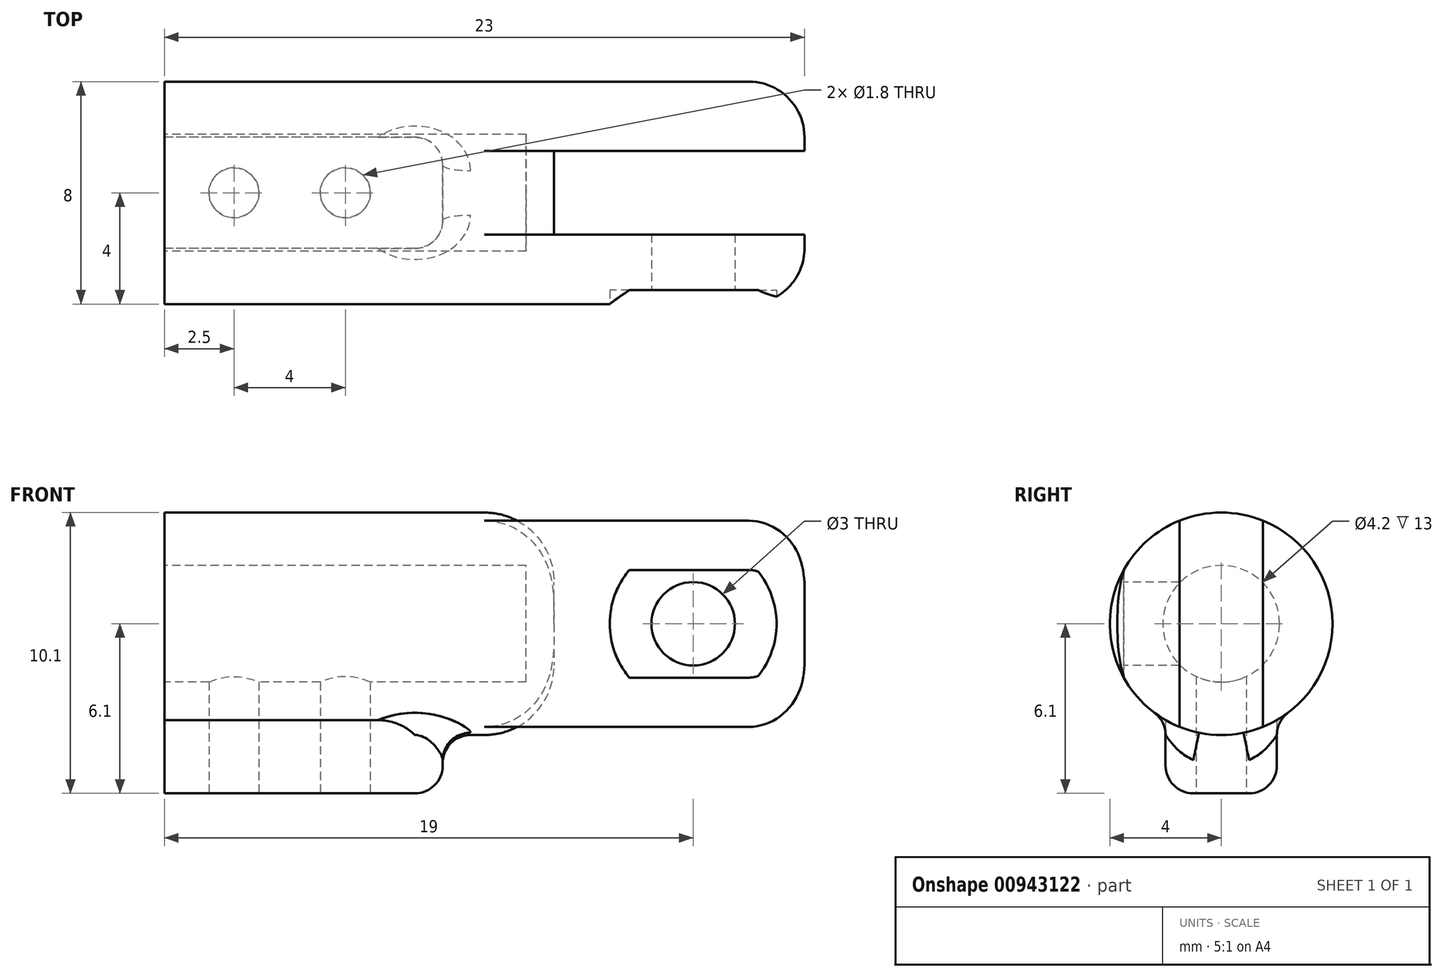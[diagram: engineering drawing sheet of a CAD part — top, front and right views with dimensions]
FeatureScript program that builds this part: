
annotation { "Feature Type Name" : "Feature", "Feature Type Description" : "" }
export const myFeature = defineFeature(function(context is Context, id is Id, definition is map)
    precondition{}
    {
        {
            var Q0;
            Q0=qCreatedBy(makeId("Right.planeOp"),FACE);
            var sketch = newSketch(context, id + "F0", { "sketchPlane" : qUnion([Q0])});
            skCircle(sketch, "E0", {"center": v(0, 0) * mm, "radius": 2.1 * mm});
            skCircle(sketch, "E1", {"center": v(0, 0) * mm, "radius": 4 * mm});
            skLineSegment(sketch, "E2", {"start": v(2, -3.46) * mm, "end": v(2, -6.1) * mm});
            skLineSegment(sketch, "E3", {"start": v(2, -6.1) * mm, "end": v(-2, -6.1) * mm});
            skLineSegment(sketch, "E4", {"start": v(-2, -6.1) * mm, "end": v(-2, -3.46) * mm});
            skSolve(sketch);
        }
        {
            var Q0;
            Q0=makeQuery(id+"F0.imprint","IMPRINT",FACE,{"disambiguationData":[TD([[makeQuery(id+"F0.imprint","IMPRINT",EDGE,{"derivedFrom":sQuery(id+"F0.wireOp",EDGE,"E0")}),-1.0]])]});
            var Q1;
            Q1=makeQuery(id+"F0.imprint","IMPRINT",FACE,{"disambiguationData":[TD([[makeQuery(id+"F0.imprint","IMPRINT",EDGE,{"derivedFrom":sQuery(id+"F0.wireOp",EDGE,"E0")}),1.0]])]});
            extrude(context, id + "F1", {"entities" : qUnion([Q0, Q1]), "depth" : 23 * mm, "offsetDistance" : 25 * mm});
        }
        {
            var Q0;
            Q0=makeQuery(id+"F0.imprint","IMPRINT",FACE,{"disambiguationData":[TD([[makeQuery(id+"F0.imprint","IMPRINT",EDGE,{"derivedFrom":sQuery(id+"F0.wireOp",EDGE,"E0")}),1.0]])]});
            extrude(context, id + "F2", {"entities" : qUnion([Q0]), "operationType" : NewBodyOperationType.REMOVE, "depth" : 13 * mm, "offsetDistance" : 25 * mm});
        }
        {
            var Q0;
            Q0=makeQuery(id+"F1.opExtrude","CAP_FACE",FACE,{"disambiguationData":[OSD([sQuery(id+"F0.wireOp",EDGE,"E0"),sQuery(id+"F0.wireOp",EDGE,"E1")])],"isStart":false});
            cPlane(context, id + "F3", {"entities" : qUnion([Q0]), "cplaneType" : CPlaneType.OFFSET, "offset" : 0 * mm, "width" : 150 * mm, "height" : 150 * mm});
        }
        {
            var Q0;
            Q0=qCreatedBy(id+"F3.planeOp",FACE);
            var sketch = newSketch(context, id + "F4", { "sketchPlane" : qUnion([Q0])});
            skLineSegment(sketch, "E5.bottom", {"start": v(1.5, -4) * mm, "end": v(-1.5, -4) * mm});
            skLineSegment(sketch, "E5.top", {"start": v(1.5, 4) * mm, "end": v(-1.5, 4) * mm});
            skLineSegment(sketch, "E5.left", {"start": v(1.5, -4) * mm, "end": v(1.5, 4) * mm});
            skLineSegment(sketch, "E5.right", {"start": v(-1.5, -4) * mm, "end": v(-1.5, 4) * mm});
            skPoint(sketch, "E5.middle", {"position": v(0, 0) * mm});
            skSolve(sketch);
        }
        {
            var Q0;
            {var subQ0=sQuery(id+"F4.wireOp",EDGE,"E5.left");var subQ1=sQuery(id+"F6oWoKsDEnx1sjk_1.wireOp",EDGE,"171556a4-600e-4862-a10e-88d223d029910.MirrorCS");var subQ2=sQuery(id+"F6oWoKsDEnx1sjk_1.wireOp",EDGE,"nGa1sqjB-H7Ow-3scy-iZwB-qixYv0Jmrafc.right");var subQ3=makeQuery(id+"FhGqZDnQz9BZsxH_1.opLoft","MID_CAP_EDGE",EDGE,{"disambiguationData":[OSD([subQ2,subQ1,sQuery(id+"F6oWoKsDEnx1sjk_1.wireOp",EDGE,"QtEZCRTN-AAdx-a9Je-NfUg-qH4uqyxohC3w")])],"capPos":1.0});var subQ4=makeQuery(id+"F4.imprint","INTERSECT",VERTEX,{"derivedFrom":[subQ3,subQ0]});Q0=makeQuery(id+"F4.imprint","IMPRINT",FACE,{"disambiguationData":[TD([[makeQuery(id+"F4.imprint","IMPRINT",EDGE,{"disambiguationData":[TD([[subQ4,-1.0]])],"derivedFrom":subQ0}),1.0]])]});}
            var Q1;
            {var subQ0=sQuery(id+"F4.wireOp",EDGE,"E5.top");Q1=makeQuery(id+"F4.imprint","IMPRINT",FACE,{"disambiguationData":[TD([[makeQuery(id+"F4.imprint","IMPRINT",EDGE,{"derivedFrom":subQ0}),1.0]])]});}
            var Q2;
            {var subQ0=sQuery(id+"F4.wireOp",EDGE,"E5.bottom");Q2=makeQuery(id+"F4.imprint","IMPRINT",FACE,{"disambiguationData":[TD([[makeQuery(id+"F4.imprint","IMPRINT",EDGE,{"derivedFrom":subQ0}),-1.0]])]});}
            extrude(context, id + "F5", {"entities" : qUnion([Q0, Q1, Q2]), "operationType" : NewBodyOperationType.REMOVE, "oppositeDirection" : true, "depth" : 9 * mm, "offsetDistance" : 25 * mm});
        }
        {
            var Q0;
            {var subQ0=sQuery(id+"F0.wireOp",EDGE,"E1");Q0=makeQuery(id+"F5.boolean.opBoolean","SPLIT",EDGE,{"disambiguationData":[TD([makeQuery(id+"F5.opExtrude","SWEPT_FACE",FACE,{"disambiguationData":[OSD([sQuery(id+"F4.wireOp",EDGE,"E5.right")])]})])],"derivedFrom":makeQuery(id+"F1.opExtrude","CAP_EDGE",EDGE,{"disambiguationData":[OSD([subQ0])],"isStart":false})});}
            cPoint(context, id + "F6", {"entities" : qUnion([Q0]), "parameter" : 0.5});
        }
        {
            var Q0;
            Q0=qCreatedBy(makeId("Front.planeOp"),FACE);
            var Q1;
            Q1=qCreatedBy(id+"F6",VERTEX);
            cPlane(context, id + "F7", {"entities" : qUnion([Q0, Q1]), "cplaneType" : CPlaneType.PLANE_POINT, "offset" : 10 * mm, "width" : 150 * mm, "height" : 150 * mm});
        }
        {
            var Q0;
            Q0=qCreatedBy(id+"F7.planeOp",FACE);
            var sketch = newSketch(context, id + "F8", { "sketchPlane" : qUnion([Q0])});
            skPoint(sketch, "E6", {"position": v(19, 0) * mm});
            skSolve(sketch);
        }
        {
            var Q0;
            Q0=sQuery(id+"F8.wireOp",VERTEX,"E6");
            var Q1;
            Q1=makeQuery(id+"F1.opExtrude","SWEPT_BODY",BODY,{"disambiguationData":[OSD([sQuery(id+"F0.wireOp",EDGE,"E1")])]});
            hole(context, id + "F9", {"style" : HoleStyle.C_BORE, "endStyle" : HoleEndStyle.BLIND, "holeDiameter" : 3 * mm, "cBoreDiameter" : 6 * mm, "cBoreDepth" : 0.5 * mm, "majorDiameter" : 5 * mm, "holeDepth" : 3 * mm, "isTappedThrough" : true, "tappedDepth" : 12 * mm, "tapClearance" : 3, "startFromSketch" : true, "locations" : qUnion([Q0]), "scope" : qUnion([Q1])});
        }
        {
            var Q0;
            Q0=makeQuery(id+"F5.boolean.opBoolean","INTERSECT",EDGE,{"disambiguationData":[OD(0.0)],"derivedFrom":[makeQuery(id+"F1.opExtrude","SWEPT_FACE",FACE,{"disambiguationData":[OSD([sQuery(id+"F0.wireOp",EDGE,"E1")])]}),makeQuery(id+"F5.opExtrude","CAP_FACE",FACE,{"disambiguationData":[OSD([sQuery(id+"F4.wireOp",EDGE,"E5.bottom"),sQuery(id+"F4.wireOp",EDGE,"E5.top"),sQuery(id+"F4.wireOp",EDGE,"E5.left"),sQuery(id+"F4.wireOp",EDGE,"E5.right")])],"isStart":false})]});
            var Q1;
            Q1=makeQuery(id+"F5.boolean.opBoolean","INTERSECT",EDGE,{"disambiguationData":[OD(1.0)],"derivedFrom":[makeQuery(id+"F1.opExtrude","SWEPT_FACE",FACE,{"disambiguationData":[OSD([sQuery(id+"F0.wireOp",EDGE,"E1")])]}),makeQuery(id+"F5.opExtrude","CAP_FACE",FACE,{"disambiguationData":[OSD([sQuery(id+"F4.wireOp",EDGE,"E5.bottom"),sQuery(id+"F4.wireOp",EDGE,"E5.top"),sQuery(id+"F4.wireOp",EDGE,"E5.left"),sQuery(id+"F4.wireOp",EDGE,"E5.right")])],"isStart":false})]});
            fillet(context, id + "F10", {"entities" : qUnion([Q0, Q1]), "radius" : 2.5 * mm, "tangentPropagation" : true, "allowEdgeOverflow" : false});
        }
        {
            var Q0;
            {var subQ0=sQuery(id+"F0.wireOp",EDGE,"E1");Q0=makeQuery(id+"F5.boolean.opBoolean","SPLIT",EDGE,{"disambiguationData":[TD([makeQuery(id+"F5.opExtrude","SWEPT_FACE",FACE,{"disambiguationData":[OSD([sQuery(id+"F4.wireOp",EDGE,"E5.left")])]})])],"derivedFrom":makeQuery(id+"F1.opExtrude","CAP_EDGE",EDGE,{"disambiguationData":[OSD([subQ0])],"isStart":false})});}
            var Q1;
            {var subQ0=sQuery(id+"F0.wireOp",EDGE,"E1");Q1=makeQuery(id+"F5.boolean.opBoolean","SPLIT",EDGE,{"disambiguationData":[TD([makeQuery(id+"F5.opExtrude","SWEPT_FACE",FACE,{"disambiguationData":[OSD([sQuery(id+"F4.wireOp",EDGE,"E5.right")])]})])],"derivedFrom":makeQuery(id+"F1.opExtrude","CAP_EDGE",EDGE,{"disambiguationData":[OSD([subQ0])],"isStart":false})});}
            fillet(context, id + "F11", {"entities" : qUnion([Q0, Q1]), "radius" : 2 * mm, "tangentPropagation" : true, "allowEdgeOverflow" : false});
        }
        {
            var Q0;
            {var subQ0=sQuery(id+"F0.wireOp",EDGE,"E2");Q0=makeQuery(id+"F0.imprint","IMPRINT",FACE,{"disambiguationData":[TD([[makeQuery(id+"F0.imprint","IMPRINT",EDGE,{"derivedFrom":subQ0}),-1.0]])]});}
            extrude(context, id + "F12", {"entities" : qUnion([Q0]), "operationType" : NewBodyOperationType.ADD, "depth" : 10 * mm, "offsetDistance" : 25 * mm});
        }
        {
            var Q0;
            Q0=makeQuery(id+"F12.opExtrude","SWEPT_FACE",FACE,{"disambiguationData":[OSD([sQuery(id+"F0.wireOp",EDGE,"E3")])]});
            var sketch = newSketch(context, id + "F13", { "sketchPlane" : qUnion([Q0])});
            skPoint(sketch, "E7", {"position": v(2.5, 0) * mm});
            skPoint(sketch, "E8", {"position": v(6.5, 0) * mm});
            skSolve(sketch);
        }
        {
            var Q0;
            Q0=sQuery(id+"F13.wireOp",VERTEX,"E7");
            var Q1;
            Q1=sQuery(id+"F13.wireOp",VERTEX,"E8");
            var Q2;
            Q2=makeQuery(id+"F1.opExtrude","SWEPT_BODY",BODY,{"disambiguationData":[OSD([sQuery(id+"F0.wireOp",EDGE,"E1")])]});
            hole(context, id + "F14", {"style" : HoleStyle.SIMPLE, "endStyle" : HoleEndStyle.BLIND, "holeDiameter" : 1.8 * mm, "majorDiameter" : 5 * mm, "holeDepth" : 5 * mm, "isTappedThrough" : true, "tappedDepth" : 12 * mm, "tapClearance" : 3, "locations" : qUnion([Q0, Q1]), "scope" : qUnion([Q2])});
        }
        {
            var Q0;
            Q0=makeQuery(id+"F12.opExtrude","SWEPT_EDGE",EDGE,{"disambiguationData":[OSD([sQuery(id+"F0.wireOp",EDGE,"E3"),sQuery(id+"F0.wireOp",EDGE,"E4")])]});
            var Q1;
            Q1=makeQuery(id+"F12.opExtrude","SWEPT_EDGE",EDGE,{"disambiguationData":[OSD([sQuery(id+"F0.wireOp",EDGE,"E2"),sQuery(id+"F0.wireOp",EDGE,"E3")])]});
            var Q2;
            Q2=makeQuery(id+"F12.opExtrude","SWEPT_EDGE",EDGE,{"disambiguationData":[OSD([sQuery(id+"F0.wireOp",EDGE,"E1"),sQuery(id+"F0.wireOp",EDGE,"E4")])]});
            var Q3;
            Q3=makeQuery(id+"F12.opExtrude","SWEPT_EDGE",EDGE,{"disambiguationData":[OSD([sQuery(id+"F0.wireOp",EDGE,"E1"),sQuery(id+"F0.wireOp",EDGE,"E2")])]});
            fillet(context, id + "F15", {"entities" : qUnion([Q0, Q1, Q2, Q3]), "radius" : 1 * mm, "tangentPropagation" : true, "allowEdgeOverflow" : false});
        }
        {
            var Q0;
            Q0=makeQuery(id+"F12.opExtrude","CAP_FACE",FACE,{"disambiguationData":[OSD([sQuery(id+"F0.wireOp",EDGE,"E1"),sQuery(id+"F0.wireOp",EDGE,"E2"),sQuery(id+"F0.wireOp",EDGE,"E3"),sQuery(id+"F0.wireOp",EDGE,"E4")])],"isStart":false});
            fillet(context, id + "F16", {"entities" : qUnion([Q0]), "radius" : 1 * mm, "tangentPropagation" : true, "allowEdgeOverflow" : false});
        }
    });
